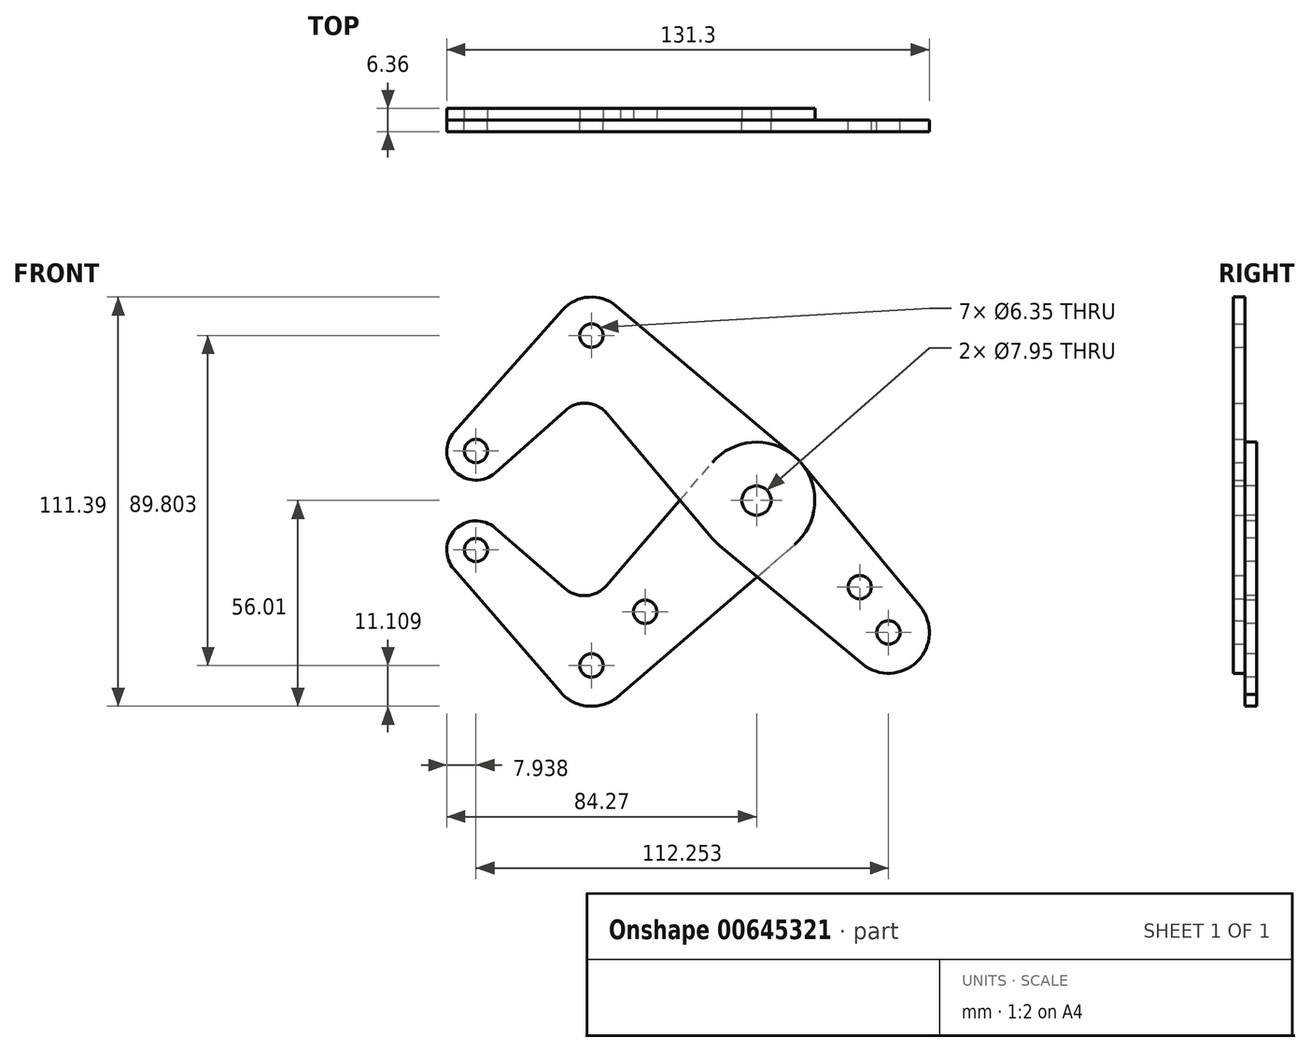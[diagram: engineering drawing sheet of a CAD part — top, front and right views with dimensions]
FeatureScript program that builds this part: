
annotation { "Feature Type Name" : "Feature", "Feature Type Description" : "" }
export const myFeature = defineFeature(function(context is Context, id is Id, definition is map)
    precondition{}
    {
        {
            var Q0;
            Q0=qCreatedBy(makeId("Front.planeOp"),FACE);
            var sketch = newSketch(context, id + "F0", { "sketchPlane" : qUnion([Q0])});
            skCircle(sketch, "E0", {"center": v(0, 0) * mm, "radius": 3.98 * mm});
            skCircle(sketch, "E1", {"center": v(35.92, -35.92) * mm, "radius": 3.18 * mm});
            skCircle(sketch, "E2", {"center": v(35.92, -35.92) * mm, "radius": 11.11 * mm});
            skCircle(sketch, "E3", {"center": v(0, 0) * mm, "radius": 3.18 * mm});
            skCircle(sketch, "E4", {"center": v(0, 0) * mm, "radius": 15.88 * mm});
            skLineSegment(sketch, "E5", {"start": v(35.92, -35.92) * mm, "end": v(0, 0) * mm, "construction": true});
            skLineSegment(sketch, "E6", {"start": v(0, 0) * mm, "end": v(-44.9, 44.9) * mm, "construction": true});
            skCircle(sketch, "E7", {"center": v(-44.9, 44.9) * mm, "radius": 3.18 * mm});
            skCircle(sketch, "E8", {"center": v(-44.9, 44.9) * mm, "radius": 10.48 * mm});
            skLineSegment(sketch, "E9", {"start": v(-44.9, 44.9) * mm, "end": v(-76.33, 13.47) * mm, "construction": true});
            skCircle(sketch, "E10", {"center": v(-76.33, 13.47) * mm, "radius": 3.18 * mm});
            skCircle(sketch, "E11", {"center": v(-76.33, 13.47) * mm, "radius": 7.94 * mm});
            skLineSegment(sketch, "E12", {"start": v(0, 0) * mm, "end": v(-44.9, -44.9) * mm, "construction": true});
            skCircle(sketch, "E13", {"center": v(-44.9, -44.9) * mm, "radius": 3.18 * mm});
            skCircle(sketch, "E14", {"center": v(-44.9, -44.9) * mm, "radius": 11.11 * mm});
            skLineSegment(sketch, "E15", {"start": v(-44.9, -44.9) * mm, "end": v(-76.33, -13.47) * mm, "construction": true});
            skCircle(sketch, "E16", {"center": v(-76.33, -13.47) * mm, "radius": 3.18 * mm});
            skCircle(sketch, "E17", {"center": v(-76.33, -13.47) * mm, "radius": 7.94 * mm});
            skCircle(sketch, "E18", {"center": v(28.07, -23.58) * mm, "radius": 3.18 * mm});
            skCircle(sketch, "E19", {"center": v(-30.3, -30.3) * mm, "radius": 3.18 * mm});
            skLineSegment(sketch, "E20", {"start": v(12.23, 10.12) * mm, "end": v(44.48, -28.83) * mm});
            skLineSegment(sketch, "E21", {"start": v(-10.12, -12.23) * mm, "end": v(28.83, -44.48) * mm});
            skLineSegment(sketch, "E22", {"start": v(-38.15, 52.91) * mm, "end": v(10.23, 12.14) * mm});
            skLineSegment(sketch, "E23", {"start": v(-40.7, 23.66) * mm, "end": v(-12.14, -10.23) * mm});
            skLineSegment(sketch, "E24", {"start": v(-82.26, 18.75) * mm, "end": v(-52.72, 51.87) * mm});
            skLineSegment(sketch, "E25", {"start": v(-71.05, 7.55) * mm, "end": v(-52.07, 24.47) * mm});
            skLineSegment(sketch, "E26", {"start": v(-71.13, -7.47) * mm, "end": v(-52.08, -23.98) * mm});
            skLineSegment(sketch, "E27", {"start": v(-82.33, -18.67) * mm, "end": v(-53.3, -52.18) * mm});
            skArc(sketch, "E28.filletArc", {"start": v(-40.7, 23.66) * mm, "mid": v(-46.21, 26.47) * mm, "end": v(-52.07, 24.47) * mm});
            skLineSegment(sketch, "E29", {"start": v(-40.85, -23.15) * mm, "end": v(-12.04, 10.35) * mm});
            skLineSegment(sketch, "E30", {"start": v(-37.66, -53.33) * mm, "end": v(10.35, -12.04) * mm});
            skArc(sketch, "E31.filletArc", {"start": v(-52.08, -23.98) * mm, "mid": v(-46.3, -25.9) * mm, "end": v(-40.85, -23.15) * mm});
            skLineSegment(sketch, "E32", {"start": v(-76.33, 13.47) * mm, "end": v(-76.33, -13.47) * mm, "construction": true});
            skLineSegment(sketch, "E33", {"start": v(0, 0) * mm, "end": v(13.33, 13.33) * mm});
            skLineSegment(sketch, "E34", {"start": v(-44.9, -44.9) * mm, "end": v(-33.74, -56.07) * mm});
            skSolve(sketch);
        }
        {
            var Q0;
            Q0=makeQuery(id+"F0.imprint","IMPRINT",FACE,{"disambiguationData":[TD([[makeQuery(id+"F0.imprint","IMPRINT",EDGE,{"derivedFrom":sQuery(id+"F0.wireOp",EDGE,"E7")}),-1.0]])]});
            var Q1;
            Q1=makeQuery(id+"F0.imprint","IMPRINT",FACE,{"disambiguationData":[TD([[makeQuery(id+"F0.imprint","IMPRINT",EDGE,{"derivedFrom":sQuery(id+"F0.wireOp",EDGE,"E10")}),-1.0]])]});
            var Q2;
            {var subQ0=sQuery(id+"F0.wireOp",EDGE,"E22");Q2=makeQuery(id+"F0.imprint","IMPRINT",FACE,{"disambiguationData":[TD([[makeQuery(id+"F0.imprint","IMPRINT",EDGE,{"derivedFrom":subQ0}),-1.0]])]});}
            var Q3;
            Q3=makeQuery(id+"F0.imprint","IMPRINT",FACE,{"disambiguationData":[TD([[makeQuery(id+"F0.imprint","IMPRINT",EDGE,{"derivedFrom":sQuery(id+"F0.wireOp",EDGE,"E0")}),-1.0]])]});
            var Q4;
            Q4=makeQuery(id+"F0.imprint","IMPRINT",FACE,{"disambiguationData":[TD([[makeQuery(id+"F0.imprint","IMPRINT",EDGE,{"derivedFrom":sQuery(id+"F0.wireOp",EDGE,"E18")}),-1.0]])]});
            var Q5;
            Q5=makeQuery(id+"F0.imprint","IMPRINT",FACE,{"disambiguationData":[TD([[makeQuery(id+"F0.imprint","IMPRINT",EDGE,{"derivedFrom":sQuery(id+"F0.wireOp",EDGE,"E1")}),-1.0]])]});
            var Q6;
            {var subQ0=sQuery(id+"F0.wireOp",EDGE,"E23");var subQ1=sQuery(id+"F0.wireOp",EDGE,"E4");var subQ2=makeQuery(id+"F0.imprint","INTERSECT",VERTEX,{"derivedFrom":[subQ1,subQ0]});Q6=makeQuery(id+"F0.imprint","IMPRINT",FACE,{"disambiguationData":[TD([[makeQuery(id+"F0.imprint","IMPRINT",EDGE,{"disambiguationData":[TD([[subQ2,1.0]])],"derivedFrom":subQ1}),-1.0]])]});}
            var Q7;
            {var subQ0=sQuery(id+"F0.wireOp",EDGE,"E21");var subQ1=sQuery(id+"F0.wireOp",EDGE,"E4");var subQ2=makeQuery(id+"F0.imprint","INTERSECT",VERTEX,{"derivedFrom":[subQ1,subQ0]});Q7=makeQuery(id+"F0.imprint","IMPRINT",FACE,{"disambiguationData":[TD([[makeQuery(id+"F0.imprint","IMPRINT",EDGE,{"disambiguationData":[TD([[subQ2,-1.0]])],"derivedFrom":subQ1}),-1.0]])]});}
            extrude(context, id + "F1", {"entities" : qUnion([Q0, Q1, Q2, Q3, Q4, Q5, Q6, Q7]), "depth" : 3.17 * mm, "offsetDistance" : 25.4 * mm});
        }
        {
            var Q0;
            Q0=makeQuery(id+"F0.imprint","IMPRINT",FACE,{"disambiguationData":[TD([[makeQuery(id+"F0.imprint","IMPRINT",EDGE,{"derivedFrom":sQuery(id+"F0.wireOp",EDGE,"E19")}),-1.0]])]});
            var Q1;
            Q1=makeQuery(id+"F0.imprint","IMPRINT",FACE,{"disambiguationData":[TD([[makeQuery(id+"F0.imprint","IMPRINT",EDGE,{"derivedFrom":sQuery(id+"F0.wireOp",EDGE,"E13")}),-1.0]])]});
            var Q2;
            Q2=makeQuery(id+"F0.imprint","IMPRINT",FACE,{"disambiguationData":[TD([[makeQuery(id+"F0.imprint","IMPRINT",EDGE,{"derivedFrom":sQuery(id+"F0.wireOp",EDGE,"E16")}),-1.0]])]});
            var Q3;
            Q3=makeQuery(id+"F0.imprint","IMPRINT",FACE,{"disambiguationData":[TD([[makeQuery(id+"F0.imprint","IMPRINT",EDGE,{"derivedFrom":sQuery(id+"F0.wireOp",EDGE,"E0")}),-1.0]])]});
            var Q4;
            {var subQ0=sQuery(id+"F0.wireOp",EDGE,"E21");var subQ1=sQuery(id+"F0.wireOp",EDGE,"E4");var subQ2=makeQuery(id+"F0.imprint","INTERSECT",VERTEX,{"derivedFrom":[subQ1,subQ0]});Q4=makeQuery(id+"F0.imprint","IMPRINT",FACE,{"disambiguationData":[TD([[makeQuery(id+"F0.imprint","IMPRINT",EDGE,{"disambiguationData":[TD([[subQ2,-1.0]])],"derivedFrom":subQ1}),-1.0]])]});}
            var Q5;
            {var subQ0=sQuery(id+"F0.wireOp",EDGE,"E23");var subQ1=sQuery(id+"F0.wireOp",EDGE,"E4");var subQ2=makeQuery(id+"F0.imprint","INTERSECT",VERTEX,{"derivedFrom":[subQ1,subQ0]});Q5=makeQuery(id+"F0.imprint","IMPRINT",FACE,{"disambiguationData":[TD([[makeQuery(id+"F0.imprint","IMPRINT",EDGE,{"disambiguationData":[TD([[subQ2,1.0]])],"derivedFrom":subQ1}),-1.0]])]});}
            extrude(context, id + "F2", {"entities" : qUnion([Q0, Q1, Q2, Q3, Q4, Q5]), "oppositeDirection" : true, "depth" : 3.17 * mm, "offsetDistance" : 25.4 * mm});
        }
    });
